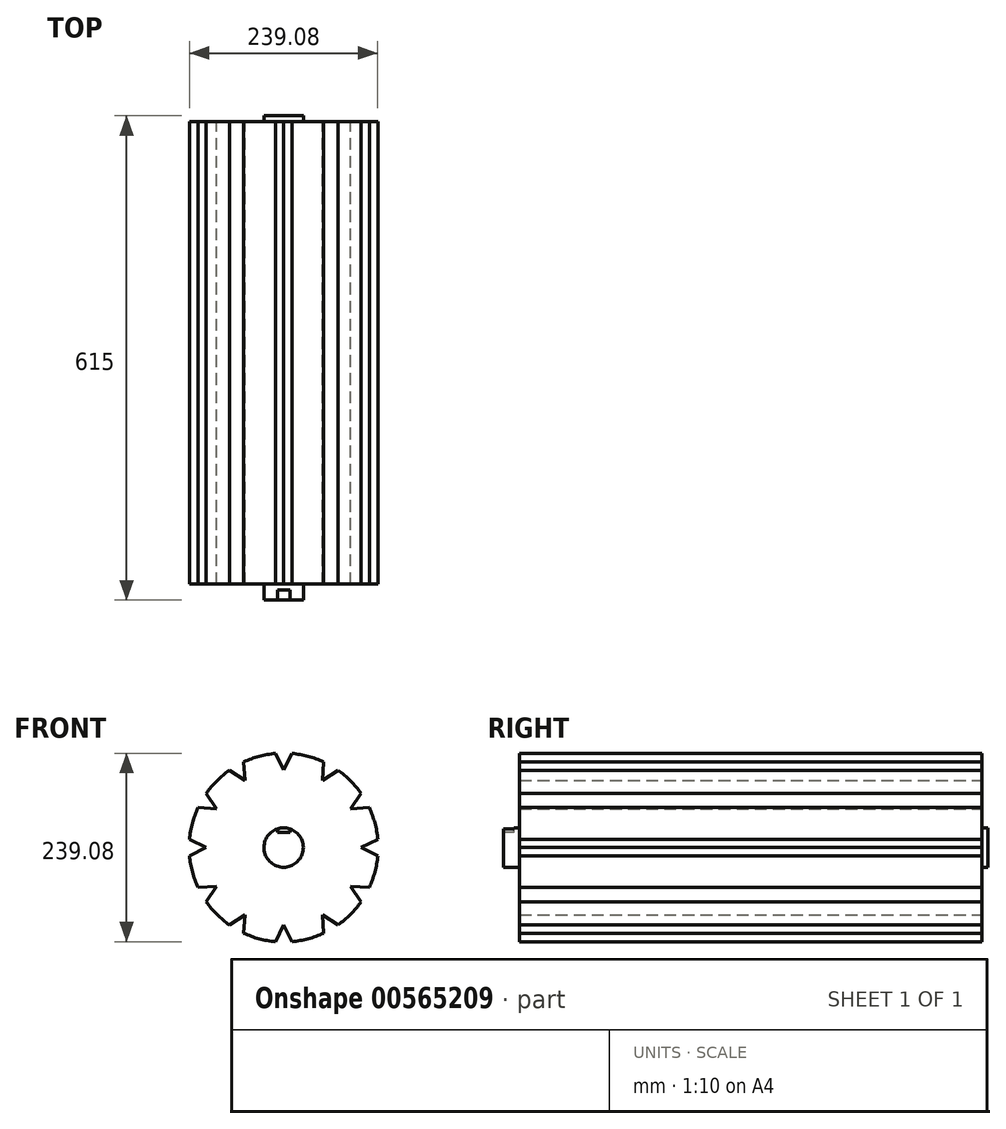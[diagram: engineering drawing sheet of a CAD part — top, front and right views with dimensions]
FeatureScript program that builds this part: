
annotation { "Feature Type Name" : "Feature", "Feature Type Description" : "" }
export const myFeature = defineFeature(function(context is Context, id is Id, definition is map)
    precondition{}
    {
        {
            var Q0;
            Q0=qCreatedBy(makeId("Front.planeOp"),FACE);
            var sketch = newSketch(context, id + "F0", { "sketchPlane" : qUnion([Q0])});
            skCircle(sketch, "E0", {"center": v(0, 0) * mm, "radius": 120 * mm});
            skLineSegment(sketch, "E1", {"start": v(-10.47, 119.54) * mm, "end": v(0, 98.4) * mm});
            skLineSegment(sketch, "E2", {"start": v(0, 0) * mm, "end": v(0, 240.15) * mm, "construction": true});
            skLineSegment(sketch, "E3.MirrorCS", {"start": v(10.47, 119.54) * mm, "end": v(0, 98.4) * mm});
            skLineSegment(sketch, "E4.1.1", {"start": v(-68.84, 98.3) * mm, "end": v(-49.2, 85.22) * mm});
            skLineSegment(sketch, "E4.1.2", {"start": v(0, 0) * mm, "end": v(-120.08, 207.98) * mm, "construction": true});
            skLineSegment(sketch, "E4.1.3", {"start": v(-50.7, 108.76) * mm, "end": v(-49.2, 85.22) * mm});
            skLineSegment(sketch, "E4.2.1", {"start": v(-108.76, 50.7) * mm, "end": v(-85.22, 49.2) * mm});
            skLineSegment(sketch, "E4.2.2", {"start": v(0, 0) * mm, "end": v(-207.98, 120.08) * mm, "construction": true});
            skLineSegment(sketch, "E4.2.3", {"start": v(-98.3, 68.84) * mm, "end": v(-85.22, 49.2) * mm});
            skLineSegment(sketch, "E4.3.1", {"start": v(-119.54, -10.47) * mm, "end": v(-98.4, 0) * mm});
            skLineSegment(sketch, "E4.3.2", {"start": v(0, 0) * mm, "end": v(-240.15, 0) * mm, "construction": true});
            skLineSegment(sketch, "E4.3.3", {"start": v(-119.54, 10.47) * mm, "end": v(-98.4, 0) * mm});
            skLineSegment(sketch, "E4.4.1", {"start": v(-98.3, -68.84) * mm, "end": v(-85.22, -49.2) * mm});
            skLineSegment(sketch, "E4.4.2", {"start": v(0, 0) * mm, "end": v(-207.98, -120.08) * mm, "construction": true});
            skLineSegment(sketch, "E4.4.3", {"start": v(-108.76, -50.7) * mm, "end": v(-85.22, -49.2) * mm});
            skLineSegment(sketch, "E4.5.1", {"start": v(-50.7, -108.76) * mm, "end": v(-49.2, -85.22) * mm});
            skLineSegment(sketch, "E4.5.2", {"start": v(0, 0) * mm, "end": v(-120.08, -207.98) * mm, "construction": true});
            skLineSegment(sketch, "E4.5.3", {"start": v(-68.84, -98.3) * mm, "end": v(-49.2, -85.22) * mm});
            skLineSegment(sketch, "E4.6.1", {"start": v(10.47, -119.54) * mm, "end": v(0, -98.4) * mm});
            skLineSegment(sketch, "E4.6.2", {"start": v(0, 0) * mm, "end": v(0, -240.15) * mm, "construction": true});
            skLineSegment(sketch, "E4.6.3", {"start": v(-10.47, -119.54) * mm, "end": v(0, -98.4) * mm});
            skLineSegment(sketch, "E4.7.1", {"start": v(68.84, -98.3) * mm, "end": v(49.2, -85.22) * mm});
            skLineSegment(sketch, "E4.7.2", {"start": v(0, 0) * mm, "end": v(120.08, -207.98) * mm, "construction": true});
            skLineSegment(sketch, "E4.7.3", {"start": v(50.7, -108.76) * mm, "end": v(49.2, -85.22) * mm});
            skLineSegment(sketch, "E4.8.1", {"start": v(108.76, -50.7) * mm, "end": v(85.22, -49.2) * mm});
            skLineSegment(sketch, "E4.8.2", {"start": v(0, 0) * mm, "end": v(207.98, -120.08) * mm, "construction": true});
            skLineSegment(sketch, "E4.8.3", {"start": v(98.3, -68.84) * mm, "end": v(85.22, -49.2) * mm});
            skLineSegment(sketch, "E4.9.1", {"start": v(119.54, 10.47) * mm, "end": v(98.4, 0) * mm});
            skLineSegment(sketch, "E4.9.2", {"start": v(0, 0) * mm, "end": v(240.15, 0) * mm, "construction": true});
            skLineSegment(sketch, "E4.9.3", {"start": v(119.54, -10.47) * mm, "end": v(98.4, 0) * mm});
            skLineSegment(sketch, "E4.10.1", {"start": v(98.3, 68.84) * mm, "end": v(85.22, 49.2) * mm});
            skLineSegment(sketch, "E4.10.2", {"start": v(0, 0) * mm, "end": v(207.98, 120.08) * mm, "construction": true});
            skLineSegment(sketch, "E4.10.3", {"start": v(108.76, 50.7) * mm, "end": v(85.22, 49.2) * mm});
            skLineSegment(sketch, "E4.11.1", {"start": v(50.7, 108.76) * mm, "end": v(49.2, 85.22) * mm});
            skLineSegment(sketch, "E4.11.2", {"start": v(0, 0) * mm, "end": v(120.08, 207.98) * mm, "construction": true});
            skLineSegment(sketch, "E4.11.3", {"start": v(68.84, 98.3) * mm, "end": v(49.2, 85.22) * mm});
            skSolve(sketch);
        }
        {
            var Q0;
            {var subQ15=sQuery(id+"F0.wireOp",EDGE,"E1");Q0=makeQuery(id+"F0.imprint","IMPRINT",FACE,{"disambiguationData":[TD([[makeQuery(id+"F0.imprint","IMPRINT",EDGE,{"derivedFrom":subQ15}),-1.0]])]});}
            extrude(context, id + "F1", {"entities" : qUnion([Q0]), "depth" : 587.5 * mm, "offsetDistance" : 25.4 * mm});
        }
        {
            var Q0;
            Q0=makeQuery(id+"F1.opExtrude","CAP_FACE",FACE,{"disambiguationData":[OSD([sQuery(id+"F0.wireOp",EDGE,"E1"),sQuery(id+"F0.wireOp",EDGE,"E3.MirrorCS"),sQuery(id+"F0.wireOp",EDGE,"E4.1.1"),sQuery(id+"F0.wireOp",EDGE,"E4.1.3"),sQuery(id+"F0.wireOp",EDGE,"E4.2.1"),sQuery(id+"F0.wireOp",EDGE,"E4.2.3"),sQuery(id+"F0.wireOp",EDGE,"E4.3.1"),sQuery(id+"F0.wireOp",EDGE,"E4.3.3"),sQuery(id+"F0.wireOp",EDGE,"E4.4.1"),sQuery(id+"F0.wireOp",EDGE,"E4.4.3"),sQuery(id+"F0.wireOp",EDGE,"E4.5.1"),sQuery(id+"F0.wireOp",EDGE,"E4.5.3"),sQuery(id+"F0.wireOp",EDGE,"E4.6.1"),sQuery(id+"F0.wireOp",EDGE,"E4.6.3"),sQuery(id+"F0.wireOp",EDGE,"E4.7.1"),sQuery(id+"F0.wireOp",EDGE,"E4.7.3"),sQuery(id+"F0.wireOp",EDGE,"E4.8.1"),sQuery(id+"F0.wireOp",EDGE,"E4.8.3"),sQuery(id+"F0.wireOp",EDGE,"E4.9.1"),sQuery(id+"F0.wireOp",EDGE,"E4.9.3"),sQuery(id+"F0.wireOp",EDGE,"E4.10.1"),sQuery(id+"F0.wireOp",EDGE,"E4.10.3"),sQuery(id+"F0.wireOp",EDGE,"E0"),sQuery(id+"F0.wireOp",EDGE,"E4.11.1"),sQuery(id+"F0.wireOp",EDGE,"E4.11.3")])],"isStart":true});
            var sketch = newSketch(context, id + "F2", { "sketchPlane" : qUnion([Q0])});
            skPoint(sketch, "E5", {"position": v(0, 0) * mm});
            skCircle(sketch, "E6", {"center": v(0, 0) * mm, "radius": 25 * mm});
            skSolve(sketch);
        }
        {
            var Q0;
            Q0=qSketchRegion(id+"F2",true);
            extrude(context, id + "F3", {"entities" : qUnion([Q0]), "operationType" : NewBodyOperationType.ADD, "depth" : 7.5 * mm, "offsetDistance" : 25.4 * mm});
        }
        {
            var Q0;
            Q0=makeQuery(id+"F1.opExtrude","CAP_FACE",FACE,{"disambiguationData":[OSD([sQuery(id+"F0.wireOp",EDGE,"E1"),sQuery(id+"F0.wireOp",EDGE,"E3.MirrorCS"),sQuery(id+"F0.wireOp",EDGE,"E4.1.1"),sQuery(id+"F0.wireOp",EDGE,"E4.1.3"),sQuery(id+"F0.wireOp",EDGE,"E4.2.1"),sQuery(id+"F0.wireOp",EDGE,"E4.2.3"),sQuery(id+"F0.wireOp",EDGE,"E4.3.1"),sQuery(id+"F0.wireOp",EDGE,"E4.3.3"),sQuery(id+"F0.wireOp",EDGE,"E4.4.1"),sQuery(id+"F0.wireOp",EDGE,"E4.4.3"),sQuery(id+"F0.wireOp",EDGE,"E4.5.1"),sQuery(id+"F0.wireOp",EDGE,"E4.5.3"),sQuery(id+"F0.wireOp",EDGE,"E4.6.1"),sQuery(id+"F0.wireOp",EDGE,"E4.6.3"),sQuery(id+"F0.wireOp",EDGE,"E4.7.1"),sQuery(id+"F0.wireOp",EDGE,"E4.7.3"),sQuery(id+"F0.wireOp",EDGE,"E4.8.1"),sQuery(id+"F0.wireOp",EDGE,"E4.8.3"),sQuery(id+"F0.wireOp",EDGE,"E4.9.1"),sQuery(id+"F0.wireOp",EDGE,"E4.9.3"),sQuery(id+"F0.wireOp",EDGE,"E4.10.1"),sQuery(id+"F0.wireOp",EDGE,"E4.10.3"),sQuery(id+"F0.wireOp",EDGE,"E0"),sQuery(id+"F0.wireOp",EDGE,"E4.11.1"),sQuery(id+"F0.wireOp",EDGE,"E4.11.3")])],"isStart":false});
            var sketch = newSketch(context, id + "F4", { "sketchPlane" : qUnion([Q0])});
            skCircle(sketch, "E7", {"center": v(0, 0) * mm, "radius": 25 * mm});
            skSolve(sketch);
        }
        {
            var Q0;
            Q0=makeQuery(id+"F4.imprint","IMPRINT",FACE,{"disambiguationData":[TD([[makeQuery(id+"F4.imprint","IMPRINT",EDGE,{"derivedFrom":sQuery(id+"F4.wireOp",EDGE,"E7")}),1.0]])]});
            extrude(context, id + "F5", {"entities" : qUnion([Q0]), "operationType" : NewBodyOperationType.ADD, "depth" : 20 * mm, "offsetDistance" : 25.4 * mm});
        }
        {
            var Q0;
            Q0=makeQuery(id+"F5.opExtrude","CAP_FACE",FACE,{"disambiguationData":[OSD([sQuery(id+"F4.wireOp",EDGE,"E7")])],"isStart":false});
            var sketch = newSketch(context, id + "F6", { "sketchPlane" : qUnion([Q0])});
            skLineSegment(sketch, "E8.bottom", {"start": v(-8, 19) * mm, "end": v(8, 19) * mm});
            skLineSegment(sketch, "E8.top", {"start": v(-8, 26) * mm, "end": v(8, 26) * mm});
            skLineSegment(sketch, "E8.left", {"start": v(-8, 19) * mm, "end": v(-8, 26) * mm});
            skLineSegment(sketch, "E8.right", {"start": v(8, 19) * mm, "end": v(8, 26) * mm});
            skSolve(sketch);
        }
        {
            var Q0;
            Q0=qSketchRegion(id+"F6",true);
            extrude(context, id + "F7", {"entities" : qUnion([Q0]), "operationType" : NewBodyOperationType.REMOVE, "oppositeDirection" : true, "depth" : 13 * mm, "offsetDistance" : 25.4 * mm});
        }
    });
